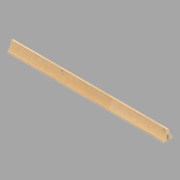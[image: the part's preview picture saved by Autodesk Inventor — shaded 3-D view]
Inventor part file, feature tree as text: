
AUTODESK INVENTOR PART (.ipt)
format: ipt  version: 2022.2 (Build 262287010, 287A)  size: 131,072 bytes
history: native  units: in
note: dims shown in document units (in); Inventor stores cm internally (conversion verified against a paired STEP export)
features: revolve x3, direct_edit x1, other x1
ambient origin geometry x8: Origin, YZ Plane, XZ Plane, XY Plane, X Axis, Y Axis, Z Axis, Center Point
bodies: Solid1 (feature_tree)
feature tree (5):
  direct_edit  "Direct Edit1"
  other  "Mull"
  revolve  "Rotate1"  [1 undecoded]
  revolve  "Rotate2"  Angle=180.0deg
  revolve  "Rotate3"  Angle=180.0deg
note: 1 required parameter value undecoded (feature->parameter linkage not recoverable at this tier; creation-order binding heuristic only, values carry confidence <= 0.55)
